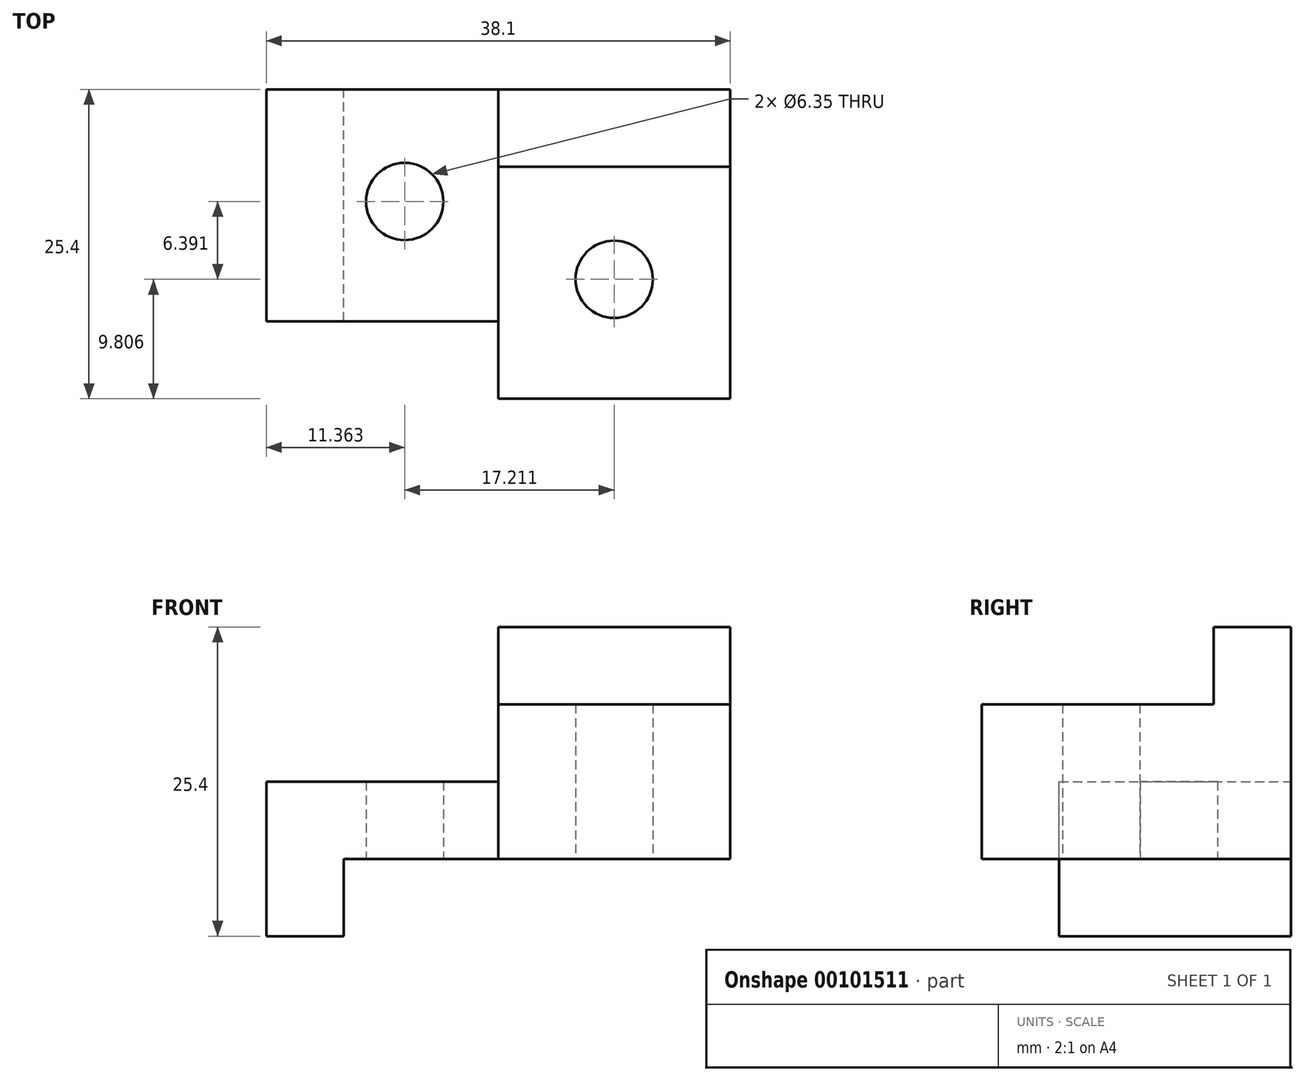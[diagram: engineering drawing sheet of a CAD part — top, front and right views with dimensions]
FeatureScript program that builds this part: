
annotation { "Feature Type Name" : "Feature", "Feature Type Description" : "" }
export const myFeature = defineFeature(function(context is Context, id is Id, definition is map)
    precondition{}
    {
        {
            var Q0;
            Q0=qCreatedBy(makeId("Front.planeOp"),FACE);
            var sketch = newSketch(context, id + "F0", { "sketchPlane" : qUnion([Q0])});
            skLineSegment(sketch, "E0.bottom", {"start": v(0, 0) * mm, "end": v(19.05, 0) * mm});
            skLineSegment(sketch, "E0.top", {"start": v(0, 19.05) * mm, "end": v(19.05, 19.05) * mm});
            skLineSegment(sketch, "E0.left", {"start": v(0, 0) * mm, "end": v(0, 19.05) * mm});
            skLineSegment(sketch, "E0.right", {"start": v(19.05, 0) * mm, "end": v(19.05, 19.05) * mm});
            skSolve(sketch);
        }
        {
            var Q0;
            Q0 = qSketchRegion(id + "F0", true);
            extrude(context, id + "F1", {"entities" : qUnion([Q0]), "depth" : 6.35 * mm});
        }
        {
            var Q0;
            Q0=qCreatedBy(makeId("Front.planeOp"),FACE);
            var sketch = newSketch(context, id + "F2", { "sketchPlane" : qUnion([Q0])});
            skLineSegment(sketch, "E1.bottom", {"start": v(0, 0) * mm, "end": v(19.05, 0) * mm});
            skLineSegment(sketch, "E1.top", {"start": v(0, 12.7) * mm, "end": v(19.05, 12.7) * mm});
            skLineSegment(sketch, "E1.left", {"start": v(0, 0) * mm, "end": v(0, 12.7) * mm});
            skLineSegment(sketch, "E1.right", {"start": v(19.05, 0) * mm, "end": v(19.05, 12.7) * mm});
            skSolve(sketch);
        }
        {
            var Q0;
            Q0 = qSketchRegion(id + "F2", true);
            extrude(context, id + "F3", {"entities" : qUnion([Q0]), "operationType" : NewBodyOperationType.ADD, "depth" : 25.4 * mm});
        }
        {
            var Q0;
            Q0=qCreatedBy(makeId("Front.planeOp"),FACE);
            var sketch = newSketch(context, id + "F4", { "sketchPlane" : qUnion([Q0])});
            skLineSegment(sketch, "E2.bottom", {"start": v(0, 0) * mm, "end": v(-19.05, 0) * mm});
            skLineSegment(sketch, "E2.top", {"start": v(0, 6.35) * mm, "end": v(-19.05, 6.35) * mm});
            skLineSegment(sketch, "E2.left", {"start": v(0, 0) * mm, "end": v(0, 6.35) * mm});
            skLineSegment(sketch, "E2.right", {"start": v(-19.05, 0) * mm, "end": v(-19.05, 6.35) * mm});
            skSolve(sketch);
        }
        {
            var Q0;
            Q0 = qSketchRegion(id + "F4", true);
            extrude(context, id + "F5", {"entities" : qUnion([Q0]), "operationType" : NewBodyOperationType.ADD, "depth" : 19.05 * mm});
        }
        {
            var Q0;
            Q0=qCreatedBy(makeId("Front.planeOp"),FACE);
            var sketch = newSketch(context, id + "F6", { "sketchPlane" : qUnion([Q0])});
            skLineSegment(sketch, "E3.bottom", {"start": v(-19.05, 0) * mm, "end": v(-12.7, 0) * mm});
            skLineSegment(sketch, "E3.top", {"start": v(-19.05, -6.35) * mm, "end": v(-12.7, -6.35) * mm});
            skLineSegment(sketch, "E3.left", {"start": v(-19.05, 0) * mm, "end": v(-19.05, -6.35) * mm});
            skLineSegment(sketch, "E3.right", {"start": v(-12.7, 0) * mm, "end": v(-12.7, -6.35) * mm});
            skSolve(sketch);
        }
        {
            var Q0;
            Q0 = qSketchRegion(id + "F6", true);
            extrude(context, id + "F7", {"entities" : qUnion([Q0]), "operationType" : NewBodyOperationType.ADD, "depth" : 19.05 * mm});
        }
        {
            var Q0;
            Q0=qCreatedBy(makeId("Top.planeOp"),FACE);
            var sketch = newSketch(context, id + "F8", { "sketchPlane" : qUnion([Q0])});
            skCircle(sketch, "E4", {"center": v(9.52, -15.6) * mm, "radius": 3.18 * mm});
            skSolve(sketch);
        }
        {
            var Q0;
            Q0 = qSketchRegion(id + "F8", true);
            var Q1;
            Q1=sQuery(id+"F8.wireOp",EDGE,"E4");
            extrude(context, id + "F9", {"entities" : qUnion([Q0]), "operationType" : NewBodyOperationType.REMOVE, "surfaceEntities" : qUnion([Q1]), "depth" : 12.7 * mm});
        }
        {
            var Q0;
            Q0=qCreatedBy(makeId("Top.planeOp"),FACE);
            var sketch = newSketch(context, id + "F10", { "sketchPlane" : qUnion([Q0])});
            skCircle(sketch, "E5", {"center": v(-7.69, -9.2) * mm, "radius": 3.17 * mm});
            skSolve(sketch);
        }
        {
            var Q0;
            Q0 = qSketchRegion(id + "F10", true);
            extrude(context, id + "F11", {"entities" : qUnion([Q0]), "operationType" : NewBodyOperationType.REMOVE, "depth" : 6.35 * mm});
        }
    });
